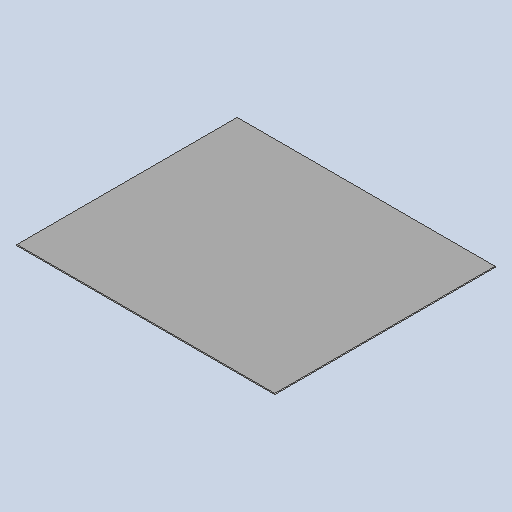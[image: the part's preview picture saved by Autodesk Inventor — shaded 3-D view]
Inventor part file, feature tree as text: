
AUTODESK INVENTOR PART (.ipt)
format: ipt  version: 2025 (Build 290162010, 162A)  size: 237,056 bytes
history: native  units: mm
features: other x5, sketch x2, sheet_metal_op x1
ambient origin geometry x8: Origin, YZ Plane, XZ Plane, XY Plane, X Axis, Y Axis, Z Axis, Center Point
bodies: Solid1 (feature_tree)
feature tree (8):
  other  "TRM 012 back main"
  sheet_metal_op  "Face1"
  other  "Mark1"
  other  "A-Side Definition"
  sketch  "Sketch1"  dims[d0=480.0mm]
  other  "Plate1"
  sketch  "Sketch2"  dims[d1=410.0mm d2=2.0mm d6=200.0mm d7=20.0mm d8=20.0mm d9=20.0mm]
  other  "Definition1"
